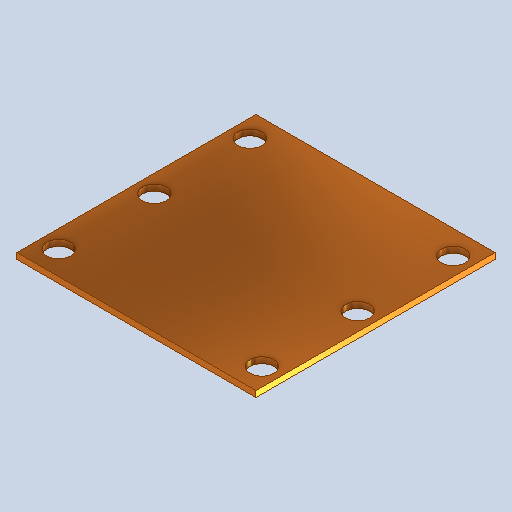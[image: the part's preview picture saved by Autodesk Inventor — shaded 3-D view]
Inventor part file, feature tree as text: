
AUTODESK INVENTOR PART (.ipt)
format: ipt  version: 2025.1 (Build 291241000, 241)  size: 247,296 bytes
history: native  units: mm
features: extrude x2, sketch x2
ambient origin geometry x8: Origin, YZ Plane, XZ Plane, XY Plane, X Axis, Y Axis, Z Axis, Center Point
bodies: Solid1 (feature_tree)
feature tree (4):
  extrude  "Extrusion1"  Depth=40.0mm
  extrude  "Extrusion2"  Depth=1.0mm
  sketch  "Sketch1"  dims[d0=40.0mm d1=40.0mm]
  sketch  "Sketch2"  dims[d2=1.0mm d3=0.0mm d4=3.0mm d5=34.0mm d6=4.0mm d7=4.0mm d8=4.0mm d9=16.0mm d10=32.0mm d11=1.0mm d12=0.0mm]
